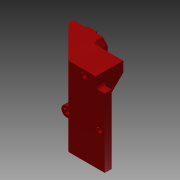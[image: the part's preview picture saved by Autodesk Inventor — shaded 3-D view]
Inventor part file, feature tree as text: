
AUTODESK INVENTOR PART (.ipt)
format: ipt  version: 2015 SP1 (Build 190203100, 203)  size: 315,392 bytes
history: native  units: in
note: dims shown in document units (in); Inventor stores cm internally (conversion verified against a paired STEP export)
features: sketch x14, extrude x9, hole x3, chamfer x3, reference x3, fillet x2
ambient origin geometry x8: Origin, YZ Plane, XZ Plane, XY Plane, X Axis, Y Axis, Z Axis, Center Point
bodies: Solid1 (feature_tree)
feature tree (34):
  sketch  "Sketch1"  dims[d0=0.7874in d1=1.5748in]
  extrude  "Extrusion1"  Depth=1.5748in
  extrude  "Extrusion6"  Depth=0.7874in
  hole  "Hole1"  [1 undecoded]
  sketch  "Sketch4"  dims[d13=0.3543in d14=0.2165in]
  extrude  "Extrusion2"  Depth=0.2165in
  extrude  "Extrusion7"  Depth=0.2461in
  extrude  "Extrusion8"  Depth=0.2461in
  fillet  "Fillet1"  Radius=0.2461in
  hole  "Hole2"  [1 undecoded]
  extrude  "Extrusion9"  Depth=0.0787in
  extrude  "Extrusion11"  Depth=0.1575in
  hole  "Hole3"  [1 undecoded]
  extrude  "Extrusion12"  Depth=0.315in TaperAngle=0.0deg
  chamfer  "Chamfer1"  [1 undecoded]
  chamfer  "Chamfer2"  Distance=0.2362in
  chamfer  "Chamfer3"  Distance=0.748in
  extrude  "Extrusion13"  Depth=0.0787in
  fillet  "Fillet4"  Radius=0.3937in
  sketch  "Sketch2"  dims[d2=0.1181in d3=0.0in d4=0.7874in]
  sketch  "Sketch3"  dims[d5=0.1772in d6=0.2362in d7=0.315in d8=0.9843in d9=90.0deg d10=0.315in d11=0.8108in d12=0.3543in]
  sketch  "Sketch5"  dims[d15=1.5748in d16=0.2461in]
  sketch  "Sketch9"  dims[d17=0.2461in d18=0.2461in d19=0.2461in]
  sketch  "Sketch10"  dims[d20=0.0394in d21=0.0in d35=45.0deg]
  sketch  "Sketch11"  dims[d37=0.0787in d38=0.0in d39=0.7874in]
  sketch  "Sketch12"  dims[d40=0.1575in d41=0.9843in]
  reference  "Reference1"
  reference  "Reference2"
  sketch  "Sketch13"  dims[d42=2.7953in d43=0.4724in]
  reference  "Reference3"
  sketch  "Sketch15"  dims[d44=0.315in d45=0.0in d46=0.315in d47=0.0in]
  sketch  "Sketch16"  dims[d48=0.0787in]
  sketch  "Sketch18"  dims[d49=0.1181in d50=0.2362in d51=0.2559in d52=0.1181in d53=90.0deg d54=0.315in d55=0.8108in d56=0.0in d57=0.0in]
  sketch  "Sketch19"  dims[d60=1.2598in d63=0.2362in d64=0.0in d69=0.748in d71=0.1181in d72=0.2362in d73=0.2559in d74=0.1181in d75=90.0deg d76=0.315in d77=0.8108in d82=0.4724in d83=0.3937in d84=0.3937in d85=0.0591in d86=0.0in d87=0.0591in d88=0.0787in d89=45.0deg d92=0.1181in d93=0.0787in d94=45.0deg d95=0.2756in d96=0.4724in d97=0.0787in d98=30.0deg d99=0.5187in d100=0.0in d101=0.0787in d102=0.1378in]
note: 4 required parameter values undecoded (feature->parameter linkage not recoverable at this tier; creation-order binding heuristic only, values carry confidence <= 0.55)
